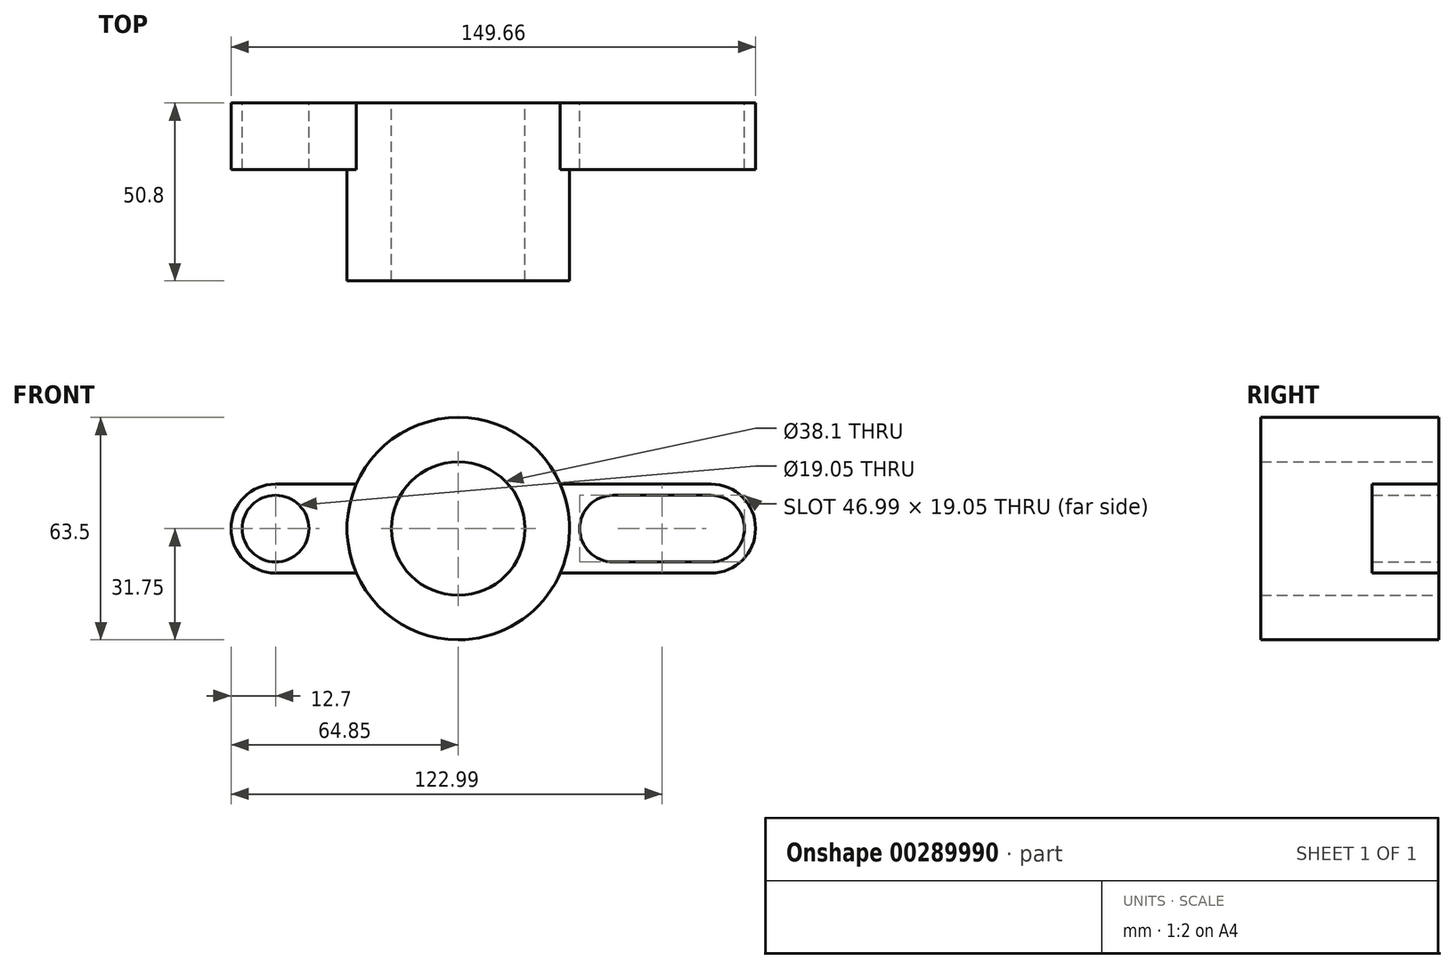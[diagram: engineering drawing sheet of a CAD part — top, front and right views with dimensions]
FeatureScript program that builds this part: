
annotation { "Feature Type Name" : "Feature", "Feature Type Description" : "" }
export const myFeature = defineFeature(function(context is Context, id is Id, definition is map)
    precondition{}
    {
        {
            var Q0;
            Q0=qCreatedBy(makeId("Front.planeOp"),FACE);
            var sketch = newSketch(context, id + "F0", { "sketchPlane" : qUnion([Q0])});
            skCircle(sketch, "E0", {"center": v(0, 0) * mm, "radius": 19.05 * mm});
            skCircle(sketch, "E1", {"center": v(0, 0) * mm, "radius": 31.75 * mm});
            skCircle(sketch, "E2", {"center": v(0, 0) * mm, "radius": 12.7 * mm});
            skArc(sketch, "E3", {"start": v(72.1, -12.7) * mm, "mid": v(84.8, 0) * mm, "end": v(72.1, 12.7) * mm});
            skArc(sketch, "E4", {"start": v(72.1, -9.53) * mm, "mid": v(81.63, 0) * mm, "end": v(72.1, 9.52) * mm});
            skArc(sketch, "E5", {"start": v(-52.15, 12.7) * mm, "mid": v(-64.85, 0) * mm, "end": v(-52.15, -12.7) * mm});
            skCircle(sketch, "E6", {"center": v(-52.15, 0) * mm, "radius": 9.53 * mm});
            skLineSegment(sketch, "E7", {"start": v(-52.15, -12.7) * mm, "end": v(-29.1, -12.7) * mm});
            skLineSegment(sketch, "E8", {"start": v(-52.15, 12.7) * mm, "end": v(-29.1, 12.7) * mm});
            skLineSegment(sketch, "E9", {"start": v(72.1, 12.7) * mm, "end": v(29.1, 12.7) * mm});
            skLineSegment(sketch, "E10", {"start": v(72.1, -12.7) * mm, "end": v(29.1, -12.7) * mm});
            skArc(sketch, "E11", {"start": v(44.17, 9.53) * mm, "mid": v(34.64, 0) * mm, "end": v(44.17, -9.53) * mm});
            skLineSegment(sketch, "E12", {"start": v(44.17, 9.53) * mm, "end": v(72.1, 9.53) * mm});
            skLineSegment(sketch, "E13", {"start": v(44.17, -9.53) * mm, "end": v(72.1, -9.53) * mm});
            skSolve(sketch);
        }
        {
            var Q0;
            Q0=makeQuery(id+"F0.imprint","IMPRINT",FACE,{"disambiguationData":[TD([[makeQuery(id+"F0.imprint","IMPRINT",EDGE,{"derivedFrom":sQuery(id+"F0.wireOp",EDGE,"E0")}),-1.0]])]});
            extrude(context, id + "F1", {"entities" : qUnion([Q0]), "depth" : 50.8 * mm});
        }
        {
            var Q0;
            Q0=makeQuery(id+"F0.imprint","IMPRINT",FACE,{"disambiguationData":[TD([[makeQuery(id+"F0.imprint","IMPRINT",EDGE,{"derivedFrom":sQuery(id+"F0.wireOp",EDGE,"E5")}),1.0]])]});
            var Q1;
            Q1=makeQuery(id+"F0.imprint","IMPRINT",FACE,{"disambiguationData":[TD([[makeQuery(id+"F0.imprint","IMPRINT",EDGE,{"derivedFrom":sQuery(id+"F0.wireOp",EDGE,"E3")}),1.0]])]});
            extrude(context, id + "F2", {"entities" : qUnion([Q0, Q1]), "operationType" : NewBodyOperationType.ADD, "depth" : 19.05 * mm});
        }
    });
